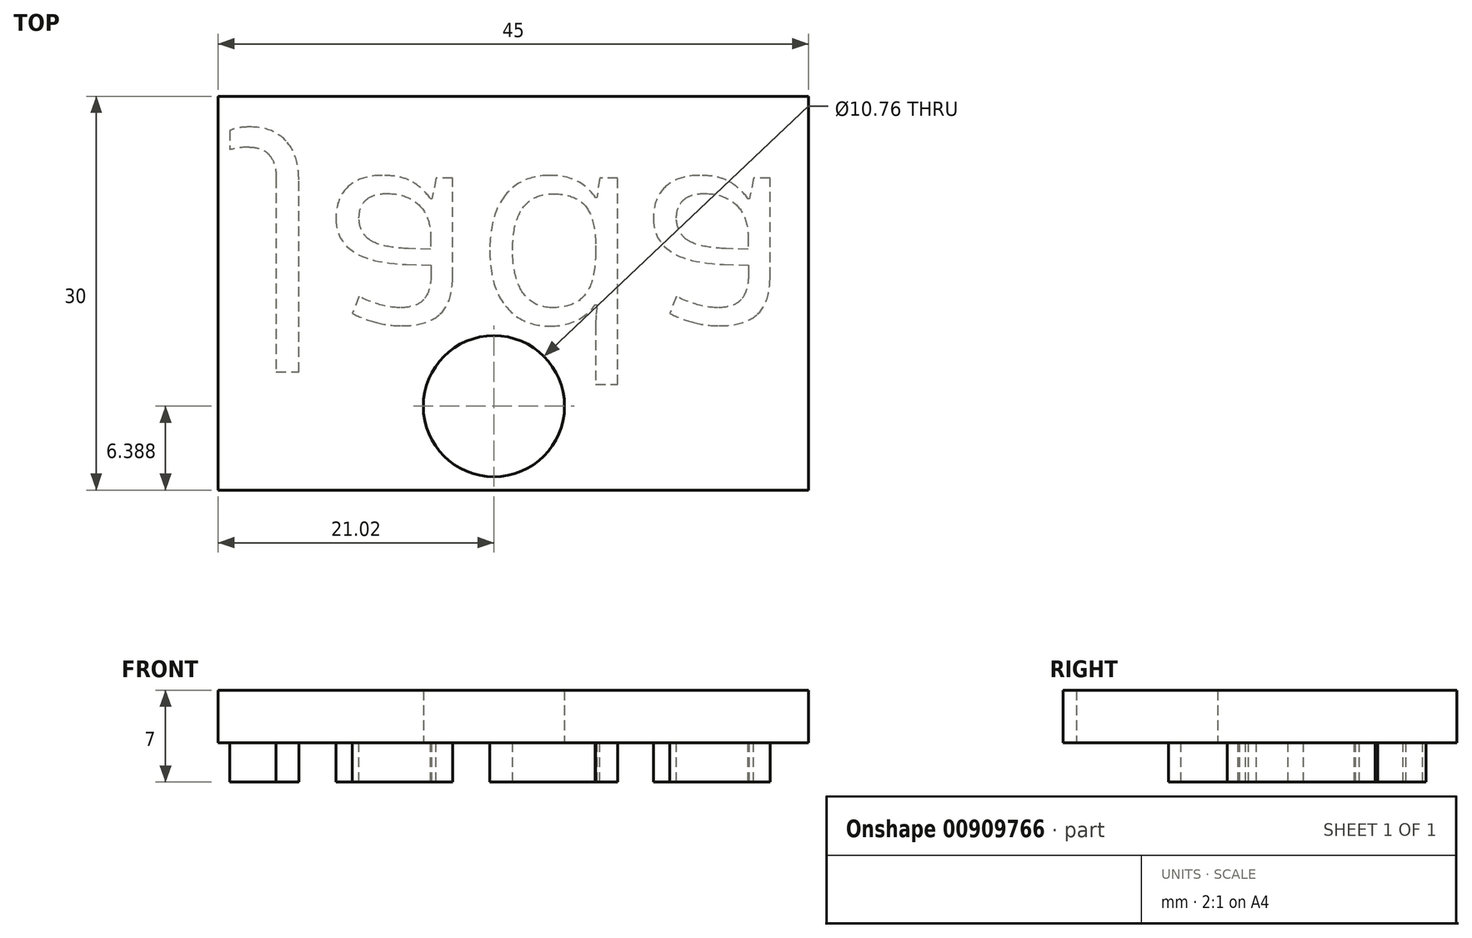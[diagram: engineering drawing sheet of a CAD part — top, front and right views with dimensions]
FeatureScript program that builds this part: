
annotation { "Feature Type Name" : "Feature", "Feature Type Description" : "" }
export const myFeature = defineFeature(function(context is Context, id is Id, definition is map)
    precondition{}
    {
        {
            var Q0;
            Q0=qCreatedBy(makeId("Top.planeOp"),FACE);
            var sketch = newSketch(context, id + "F0", { "sketchPlane" : qUnion([Q0])});
            skLineSegment(sketch, "E0.bottom", {"start": v(0, 0) * mm, "end": v(45, 0) * mm});
            skLineSegment(sketch, "E0.top", {"start": v(0, 30) * mm, "end": v(45, 30) * mm});
            skLineSegment(sketch, "E0.left", {"start": v(0, 0) * mm, "end": v(0, 30) * mm});
            skLineSegment(sketch, "E0.right", {"start": v(45, 0) * mm, "end": v(45, 30) * mm});
            skText(sketch, "E1", { "text": "Jada", "fontName": "OpenSans-Regular.ttf"});
            const initialGuessF0  = {"E1": [-0.06156, 0.05453, 1, 0, 0.01257]};
            skSetInitialGuess(sketch, initialGuessF0);
            skSolve(sketch);
        }
        {
            var Q0;
            Q0=makeQuery(id+"F0.imprint","IMPRINT",FACE,{"disambiguationData":[TD([[makeQuery(id+"F0.imprint","IMPRINT",EDGE,{"derivedFrom":sQuery(id+"F0.wireOp",EDGE,"E0.bottom")}),1.0]])]});
            extrude(context, id + "F1", {"entities" : qUnion([Q0]), "depth" : 4 * mm, "offsetDistance" : 25 * mm});
        }
        {
            var Q0;
            Q0=makeQuery(id+"F1.opExtrude","CAP_FACE",FACE,{"disambiguationData":[OSD([sQuery(id+"F0.wireOp",EDGE,"E0.bottom"),sQuery(id+"F0.wireOp",EDGE,"E0.top"),sQuery(id+"F0.wireOp",EDGE,"E0.left"),sQuery(id+"F0.wireOp",EDGE,"E0.right")])],"isStart":true});
            var sketch = newSketch(context, id + "F2", { "sketchPlane" : qUnion([Q0])});
            skText(sketch, "E2", { "text": "Jada", "fontName": "OpenSans-Regular.ttf"});
            const initialGuessF2  = {"E2": [0.00251, -0.02377, 1, 0, 0.0149]};
            skSetInitialGuess(sketch, initialGuessF2);
            skSolve(sketch);
        }
        {
            var Q0;
            Q0 = qSketchRegion(id + "F2", true);
            extrude(context, id + "F3", {"entities" : qUnion([Q0]), "operationType" : NewBodyOperationType.ADD, "depth" : 3 * mm, "offsetDistance" : 25 * mm});
        }
        {
            var Q0;
            {var subQ0=sQuery(id+"F0.wireOp",EDGE,"E0.left");var subQ1=sQuery(id+"F0.wireOp",EDGE,"E0.bottom");var subQ2=sQuery(id+"F0.wireOp",EDGE,"E0.right");var subQ3=sQuery(id+"F0.wireOp",EDGE,"E0.top");Q0=makeQuery(id+"F3.boolean.opBoolean","SPLIT",FACE,{"disambiguationData":[TD([makeQuery(id+"F1.opExtrude","SWEPT_FACE",FACE,{"disambiguationData":[OSD([subQ1])]})])],"derivedFrom":makeQuery(id+"F1.opExtrude","CAP_FACE",FACE,{"disambiguationData":[OSD([subQ1,subQ3,subQ0,subQ2])],"isStart":true})});}
            var sketch = newSketch(context, id + "F4", { "sketchPlane" : qUnion([Q0])});
            skCircle(sketch, "E3", {"center": v(20.91, -5.43) * mm, "radius": 3.19 * mm});
            skSolve(sketch);
        }
        {
            var Q0;
            Q0 = qSketchRegion(id + "F4", true);
            extrude(context, id + "F5", {"entities" : qUnion([Q0]), "operationType" : NewBodyOperationType.ADD, "oppositeDirection" : true, "depth" : 4 * mm, "offsetDistance" : 25 * mm});
        }
        {
            var Q0;
            {var subQ0=sQuery(id+"F0.wireOp",EDGE,"E0.left");var subQ1=sQuery(id+"F0.wireOp",EDGE,"E0.bottom");var subQ2=sQuery(id+"F0.wireOp",EDGE,"E0.right");var subQ3=sQuery(id+"F0.wireOp",EDGE,"E0.top");Q0=makeQuery(id+"F3.boolean.opBoolean","SPLIT",FACE,{"disambiguationData":[TD([makeQuery(id+"F1.opExtrude","SWEPT_FACE",FACE,{"disambiguationData":[OSD([subQ1])]})])],"derivedFrom":makeQuery(id+"F1.opExtrude","CAP_FACE",FACE,{"disambiguationData":[OSD([subQ1,subQ3,subQ0,subQ2])],"isStart":true})});}
            var sketch = newSketch(context, id + "F6", { "sketchPlane" : qUnion([Q0])});
            skCircle(sketch, "E4", {"center": v(21.02, -6.39) * mm, "radius": 5.38 * mm});
            skSolve(sketch);
        }
        {
            var Q0;
            Q0=makeQuery(id+"F6.imprint","IMPRINT",FACE,{"disambiguationData":[TD([[makeQuery(id+"F6.imprint","IMPRINT",EDGE,{"derivedFrom":sQuery(id+"F6.wireOp",EDGE,"E4")}),1.0]])]});
            extrude(context, id + "F7", {"entities" : qUnion([Q0]), "operationType" : NewBodyOperationType.REMOVE, "oppositeDirection" : true, "depth" : 25 * mm, "offsetDistance" : 25 * mm});
        }
    });
